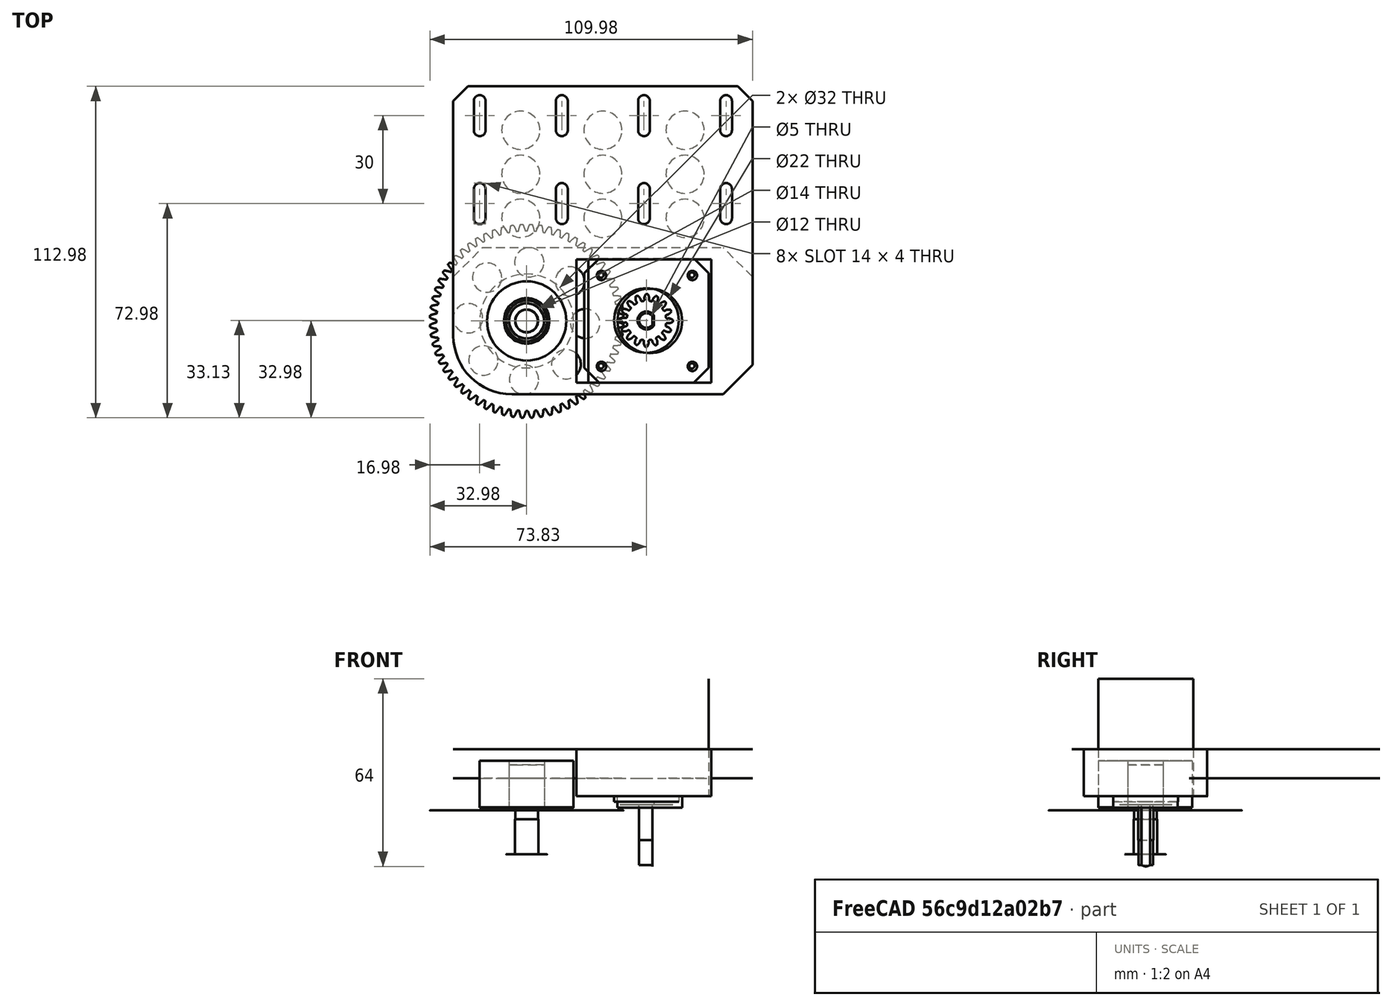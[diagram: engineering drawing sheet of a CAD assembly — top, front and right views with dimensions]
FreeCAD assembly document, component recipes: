
FREECAD ASSEMBLY — COMPONENT RECIPES ("przekladnia")

This assembly document has 7 components, labeled P0..P6 below (a component is one placed body or linked part). 3 of them carry a construction recipe — the FreeCAD feature program that regenerates the part from scratch, quoted from this document or its linked companion documents; the rest are supplied as boundary geometry only. No exploded tour is included for this assembly.
COMPONENT P0 — geometry summary ("kolkozebstozniskie"; no construction recipe available for this part):
  bounding box: 18.0 x 18.0 x 12.0 mm
  tessellated surface: 48,910 triangles
  volume: 2100 mm^3 (54% of its bounding box)
COMPONENT P1 — geometry summary ("plyta-przekadni"; no construction recipe available for this part):
  bounding box: 105.0 x 102.0 x 20.0 mm
  tessellated surface: 14,572 triangles
  volume: 91991 mm^3 (43% of its bounding box)
COMPONENT P2 — recipe-attached ("nema17", a linked part whose construction recipe lives in a companion FreeCAD document of the same project; that document's serialized recipe follows).
Construction recipe (the companion document, serialized — sketch geometry with constraints, then the solid features built on it; lengths are millimeters unless a unit is written):

FCSTD DOCUMENT  (FreeCAD 2020.10.16R22739 +2665 (Git))
Label: krokowiec-nema17
License: All rights reserved
LicenseURL: http://en.wikipedia.org/wiki/All_rights_reserved
objects: Sketcher::SketchObject×5, PartDesign::Pad×3, PartDesign::Chamfer×2, PartDesign::Pocket×1, PartDesign::Hole×1, PartDesign::Body×1
note: 27 computed .brp shape members not serialized (recipe doc carries the construction recipe); baked Part::Feature solids carry a one-line shape summary decoded from their .brp

FEATURE [Sketcher::SketchObject] Sketch
  MapMode = 5
  Support = -> [XY_Plane]
  sketch-geometry (5):
    g0: LineSegment StartX=21.15 StartY=21.15 StartZ=0 EndX=-21.15 EndY=21.15 EndZ=0
    g1: LineSegment StartX=-21.15 StartY=21.15 StartZ=0 EndX=-21.15 EndY=-21.15 EndZ=0
    g2: LineSegment StartX=-21.15 StartY=-21.15 StartZ=0 EndX=21.15 EndY=-21.15 EndZ=0
    g3: LineSegment StartX=21.15 StartY=-21.15 StartZ=0 EndX=21.15 EndY=21.15 EndZ=0
    g4: Circle [constr] CenterX=0 CenterY=0 CenterZ=0 NormalX=0 NormalY=0 NormalZ=1 AngleXU=0 Radius=29.9106
  constraints (14):
    c: Coincident(g0,g1)
    c: Coincident(g1,g2)
    c: Coincident(g2,g3)
    c: Coincident(g3,g0)
    c: Equal(g0,g1)
    c: Equal(g0,g2)
    c: Equal(g0,g3)
    c: PointOnObject(g0,g4)
    c: PointOnObject(g1,g4)
    c: PointOnObject(g2,g4)
    c: PointOnObject(g3,g4)
    c: Coincident(g4,g-1)
    c: Horizontal(g0)
    c: DistanceY(g3,g3) = 42.3
FEATURE [PartDesign::Pad] Pad
  ClaimChildren = false
  Direction = (1,1,1)
  Length = 40
  Length2 = 100
  NewSolid = false
  Profile = -> Sketch
  Suppress = false
  Type = 0
FEATURE [Sketcher::SketchObject] Sketch001
  MapMode = 5
  Placement = pos=(0,0,40) rot=(0,0,1;0rad)
  Support = -> [Pad]
  sketch-geometry (1):
    g0: Circle CenterX=0 CenterY=0 CenterZ=0 NormalX=0 NormalY=0 NormalZ=1 AngleXU=0 Radius=11
  constraints (2):
    c: Coincident(g0,g-1)
    c: Diameter(g0) = 22
FEATURE [PartDesign::Pad] Pad001
  BaseFeature = -> Pad
  ClaimChildren = false
  Direction = (1,1,1)
  Length = 2
  Length2 = 100
  NewSolid = false
  Profile = -> Sketch001
  Suppress = false
  Type = 0
FEATURE [Sketcher::SketchObject] Sketch002
  MapMode = 5
  Placement = pos=(0,0,40) rot=(0,0,1;0rad)
  Support = -> [Pad001]
  sketch-geometry (1):
    g0: Circle CenterX=0 CenterY=0 CenterZ=0 NormalX=0 NormalY=0 NormalZ=1 AngleXU=0 Radius=2.5
  constraints (2):
    c: Coincident(g0,g-1)
    c: Diameter(g0) = 5
FEATURE [PartDesign::Pad] Pad002
  BaseFeature = -> Pad001
  ClaimChildren = false
  Direction = (1,1,1)
  Length = 24
  Length2 = 100
  NewSolid = false
  Profile = -> Sketch002
  Suppress = false
  Type = 0
FEATURE [PartDesign::Chamfer] Chamfer
  Angle = 45
  Base = -> Pad002 [Edge18]
  BaseFeature = -> Pad002
  ChamferType = 0
  FlipDirection = false
  NewSolid = false
  Size = 0.5
  Size2 = 1
  SupportTransform = true
  Suppress = false
FEATURE [Sketcher::SketchObject] Sketch003
  ExternalGeometry = -> [Chamfer]
  MapMode = 5
  Placement = pos=(0,0,0) rot=(1,0,0;1.5708rad)
  Support = -> [XZ_Plane]
  sketch-geometry (4):
    g0: LineSegment StartX=2 StartY=64 StartZ=0 EndX=2.5 EndY=64 EndZ=0
    g1: LineSegment StartX=2.5 StartY=64 StartZ=0 EndX=2.5 EndY=43 EndZ=0
    g2: LineSegment StartX=2.5 StartY=43 StartZ=0 EndX=2 EndY=43 EndZ=0
    g3: LineSegment StartX=2 StartY=43 StartZ=0 EndX=2 EndY=64 EndZ=0
  constraints (12):
    c: Coincident(g0,g1)
    c: Coincident(g1,g2)
    c: Coincident(g2,g3)
    c: Coincident(g3,g0)
    c: Horizontal(g0)
    c: Horizontal(g2)
    c: Vertical(g1)
    c: Vertical(g3)
    c: PointOnObject(g0,g-3)
    c: PointOnObject(g1,g-4)
    c: DistanceX(g2,g2) = 0.5
    c: DistanceY(g1,g1) = 21
FEATURE [PartDesign::Pocket] Pocket
  BaseFeature = -> Chamfer
  ClaimChildren = false
  Length = 20
  Length2 = 100
  Midplane = true
  NewSolid = false
  Profile = -> Sketch003
  Suppress = false
  Type = 1
FEATURE [Sketcher::SketchObject] Sketch004
  MapMode = 5
  Placement = pos=(0,0,40) rot=(0,0,1;0rad)
  Support = -> [Pocket]
  sketch-geometry (4):
    g0: Circle CenterX=15.5 CenterY=-15.5 CenterZ=0 NormalX=0 NormalY=0 NormalZ=1 AngleXU=0 Radius=1.25
    g1: Circle CenterX=15.5 CenterY=15.5 CenterZ=0 NormalX=0 NormalY=0 NormalZ=1 AngleXU=0 Radius=1.25
    g2: Circle CenterX=-15.5 CenterY=15.5 CenterZ=0 NormalX=0 NormalY=0 NormalZ=1 AngleXU=0 Radius=1.25
    g3: Circle CenterX=-15.5 CenterY=-15.5 CenterZ=0 NormalX=0 NormalY=0 NormalZ=1 AngleXU=0 Radius=1.25
  constraints (9):
    c: Diameter(g0) = 2.5
    c: Symmetric(g1,g0,g-1)
    c: Symmetric(g1,g2,g-2)
    c: Symmetric(g3,g2,g-1)
    c: Equal(g2,g1)
    c: Equal(g1,g3)
    c: Equal(g3,g0)
    c: DistanceX(g2,g1) = 31
    c: DistanceY(g0,g1) = 31
FEATURE [PartDesign::Hole] Hole
  BaseFeature = -> Pocket
  ClaimChildren = false
  Depth = 4
  DepthType = 0
  Diameter = 1.75
  DrillPoint = 1
  DrillPointAngle = 118
  HoleCutCountersinkAngle = 90
  HoleCutDepth = 0
  HoleCutDiameter = 1.6
  HoleCutType = 0
  ModelActualThread = false
  NewSolid = false
  Profile = -> Sketch004
  Suppress = false
  Tapered = false
  TaperedAngle = 90
  ThreadAngle = 0
  ThreadClass = 0
  ThreadCutOffInner = 0
  ThreadCutOffOuter = 0
  ThreadDirection = 0
  ThreadFit = 0
  ThreadPitch = 0
  ThreadSize = 0
  ThreadType = 1
  Threaded = false
FEATURE [PartDesign::Chamfer] Chamfer001
  Angle = 45
  Base = -> Hole [Edge26,Edge23,Edge28,Edge24]
  BaseFeature = -> Hole
  ChamferType = 0
  FlipDirection = false
  NewSolid = false
  Size = 5
  Size2 = 1
  SupportTransform = true
  Suppress = false
FEATURE [PartDesign::Body] Body  label="nema17"
  ExportMode = 0
  Group = -> [Sketch,Pad,Sketch001,Pad001,Sketch002,Pad002,Chamfer,Sketch003,Pocket,Sketch004,Hole,Chamfer001]
  Origin = -> Origin
  Tip = -> Chamfer001
  _ExportChildren = -> [Pad,Pad001,Pad002,Chamfer,Pocket,Hole,Chamfer001]
  _GroupVersion = 1
COMPONENT P3 — geometry summary ("lozysko5201"; no construction recipe available for this part):
  bounding box: 32.0 x 32.0 x 15.9 mm
  tessellated surface: 3,024 triangles
  volume: 10222 mm^3 (63% of its bounding box)
  symmetry: 2-fold rotationally symmetric about the x axis; 2-fold rotationally symmetric about the y axis; revolution-symmetric about the z axis through its bounding-box center; mirror-symmetric across its x mid-plane, z mid-plane
COMPONENT P4 — geometry summary ("wkladkamimosr"; no construction recipe available for this part):
  bounding box: 16.5 x 14.0 x 14.0 mm
  tessellated surface: 2,016 triangles
  volume: 1121 mm^3 (35% of its bounding box)
  symmetry: 6-fold rotationally symmetric about the z axis
COMPONENT P5 — recipe-attached ("koloprzekladni", a linked part whose construction recipe lives in a companion FreeCAD document of the same project; that document's serialized recipe follows).
Construction recipe (the companion document, serialized — sketch geometry with constraints, then the solid features built on it; lengths are millimeters unless a unit is written):

FCSTD DOCUMENT  (FreeCAD 2020.10.16R22739 +2665 (Git))
Label: koloprzekladni
License: All rights reserved
LicenseURL: http://en.wikipedia.org/wiki/All_rights_reserved
objects: Sketcher::SketchObject×3, Part::FeaturePython×2, PartDesign::Groove×2, Part::Fuse×1, PartDesign::FeatureBase×1, PartDesign::Pocket×1, PartDesign::PolarPattern×1, PartDesign::Body×1
note: 20 computed .brp shape members not serialized (recipe doc carries the construction recipe); baked Part::Feature solids carry a one-line shape summary decoded from their .brp

FEATURE [Part::FeaturePython] involutegear  # WARN: FeaturePython — macro-defined, semantics opaque (R4)
  backlash = 0
  beta = 0
  clearance = 0.25
  double_helix = false
  dw = 20
  head = 0
  height = 15
  module = 1
  numpoints = 6
  pressure_angle = 20
  properties_from_tool = true
  reversed_backlash = false
  shift = 0
  simple = false
  teeth = 20
  transverse_pitch = 3.14159
  undercut = false
FEATURE [Part::FeaturePython] involutegear001  # WARN: FeaturePython — macro-defined, semantics opaque (R4)
  Placement = pos=(0,0,-10) rot=(0,0,1;0rad)
  backlash = 0
  beta = 0
  clearance = 0.25
  double_helix = false
  dw = 64
  head = 0
  height = 10
  module = 1
  numpoints = 6
  pressure_angle = 20
  properties_from_tool = true
  reversed_backlash = false
  shift = 0
  simple = false
  teeth = 64
  transverse_pitch = 3.14159
  undercut = false
FEATURE [Sketcher::SketchObject] Sketch
  MapMode = 5
  Placement = pos=(0,0,0) rot=(0.57735,0.57735,0.57735;2.0944rad)
  Support = -> [YZ_Plane]
  sketch-geometry (6):
    g0: LineSegment StartX=0 StartY=20 StartZ=0 EndX=7 EndY=20 EndZ=0
    g1: LineSegment StartX=7 StartY=20 StartZ=0 EndX=7 EndY=5 EndZ=0
    g2: LineSegment StartX=7 StartY=5 StartZ=0 EndX=3.9 EndY=5 EndZ=0
    g3: LineSegment StartX=3.9 StartY=5 StartZ=0 EndX=3.9 EndY=-20 EndZ=0
    g4: LineSegment StartX=3.9 StartY=-20 StartZ=0 EndX=0 EndY=-20 EndZ=0
    g5: LineSegment StartX=0 StartY=-20 StartZ=0 EndX=0 EndY=20 EndZ=0
  constraints (18):
    c: PointOnObject(g0,g-2)
    c: Horizontal(g0)
    c: Coincident(g0,g1)
    c: Vertical(g1)
    c: Coincident(g1,g2)
    c: Horizontal(g2)
    c: Coincident(g2,g3)
    c: Vertical(g3)
    c: Coincident(g3,g4)
    c: PointOnObject(g4,g-2)
    c: Horizontal(g4)
    c: Coincident(g4,g5)
    c: Coincident(g5,g0)
    c: DistanceX(g0) = 7
    c: DistanceY(g0) = 20
    c: DistanceX(g2) = 3.9
    c: DistanceY(g4) = -20
    c: DistanceY(g1) = 5
FEATURE [Part::Fuse] Fusion
  Base = -> involutegear
  Tool = -> involutegear001
FEATURE [PartDesign::FeatureBase] BaseFeature
  BaseFeature = -> Fusion
  NewSolid = false
  Suppress = false
FEATURE [PartDesign::Groove] Groove
  Angle = 360
  Axis = (-2e-16,3e-16,1)
  Base = (0,0,0)
  BaseFeature = -> BaseFeature
  ClaimChildren = false
  NewSolid = false
  Profile = -> Sketch
  ReferenceAxis = -> Sketch [V_Axis]
  Suppress = false
FEATURE [Sketcher::SketchObject] Sketch001
  MapMode = 5
  Placement = pos=(0,0,0) rot=(1,0,0;1.5708rad)
  Support = -> [XZ_Plane]
  sketch-geometry (4):
    g0: LineSegment StartX=-28 StartY=0 StartZ=0 EndX=-25.8162 EndY=-6 EndZ=0
    g1: LineSegment StartX=-25.8162 StartY=-6 StartZ=0 EndX=-14.1838 EndY=-6 EndZ=0
    g2: LineSegment StartX=-14.1838 StartY=-6 StartZ=0 EndX=-12 EndY=0 EndZ=0
    g3: LineSegment StartX=-12 StartY=0 StartZ=0 EndX=-28 EndY=0 EndZ=0
  constraints (12):
    c: Coincident(g0,g1)
    c: Horizontal(g1)
    c: Coincident(g1,g2)
    c: Coincident(g2,g3)
    c: Coincident(g3,g0)
    c: Horizontal(g3)
    c: DistanceY(g1) = -6
    c: DistanceX(g0) = -28
    c: DistanceX(g2) = -12
    c: DistanceY(g2) = 0
    c: Equal(g2,g0)
    c: Angle(g2,g1) = 1.91986
FEATURE [PartDesign::Groove] Groove001
  Angle = 360
  Axis = (0,-2e-16,1)
  Base = (0,0,0)
  BaseFeature = -> Groove
  ClaimChildren = false
  NewSolid = false
  Profile = -> Sketch001
  ReferenceAxis = -> Sketch001 [V_Axis]
  Reversed = true
  Suppress = false
FEATURE [Sketcher::SketchObject] Sketch002
  MapMode = 5
  Support = -> [XY_Plane]
  sketch-geometry (1):
    g0: Circle CenterX=0 CenterY=20 CenterZ=0 NormalX=0 NormalY=0 NormalZ=1 AngleXU=0 Radius=5
  constraints (3):
    c: PointOnObject(g0,g-2)
    c: Diameter(g0) = 10
    c: DistanceY(g0) = 20
FEATURE [PartDesign::Pocket] Pocket
  BaseFeature = -> Groove001
  ClaimChildren = false
  Length = 5
  Length2 = 100
  NewSolid = false
  Profile = -> Sketch002
  Suppress = false
  Type = 1
FEATURE [PartDesign::PolarPattern] PolarPattern
  Angle = 360
  Axis = -> Sketch002 [N_Axis]
  BaseFeature = -> Pocket
  CopyShape = false
  NewSolid = false
  Occurrences = 8
  OriginalSubs = -> [Pocket]
  Originals = -> [Pocket]
  SubTransform = true
  Suppress = false
FEATURE [PartDesign::Body] Body  label="koloprzekladni"
  BaseFeature = -> Fusion
  ExportMode = 0
  Group = -> [BaseFeature,Sketch,Groove,Sketch001,Groove001,Sketch002,Pocket,PolarPattern]
  Origin = -> Origin
  Tip = -> PolarPattern
  _ExportChildren = -> [BaseFeature,Groove,Groove001,Pocket,PolarPattern]
  _GroupVersion = 1
COMPONENT P6 — recipe-attached ("m8x40imb", a linked part whose construction recipe lives in a companion FreeCAD document of the same project; that document's serialized recipe follows).
Construction recipe (the companion document, serialized — sketch geometry with constraints, then the solid features built on it; lengths are millimeters unless a unit is written):

FCSTD DOCUMENT  (FreeCAD 0.19R21911 +2545 (Git))
Label: m8x40imb
License: All rights reserved
LicenseURL: http://en.wikipedia.org/wiki/All_rights_reserved
objects: Part::Feature×1, PartDesign::FeatureBase×1, PartDesign::Body×1
note: 4 computed .brp shape members not serialized (recipe doc carries the construction recipe); baked Part::Feature solids carry a one-line shape summary decoded from their .brp

FEATURE [Part::Feature] BOLTS_part  label="Hex socket head cap screw M8 40.0"
  shape: bbox 13 x 13 x 48 mm, 13 faces (baked)
FEATURE [PartDesign::FeatureBase] BaseFeature
  BaseFeature = -> BOLTS_part
  Suppress = false
FEATURE [PartDesign::Body] Body  label="m8x40imb"
  BaseFeature = -> BOLTS_part
  ExportMode = 0
  Group = -> [BaseFeature]
  Origin = -> Origin
  Tip = -> BaseFeature
  _ExportChildren = -> [BaseFeature]
  _GroupVersion = 1
PROVENANCE & LICENSES
A FreeCAD (.FCStd) document from a public repository crawl; recipes are the document's own serialized feature recipes (and, for linked parts, companion documents' recipes).
License: bsd.
